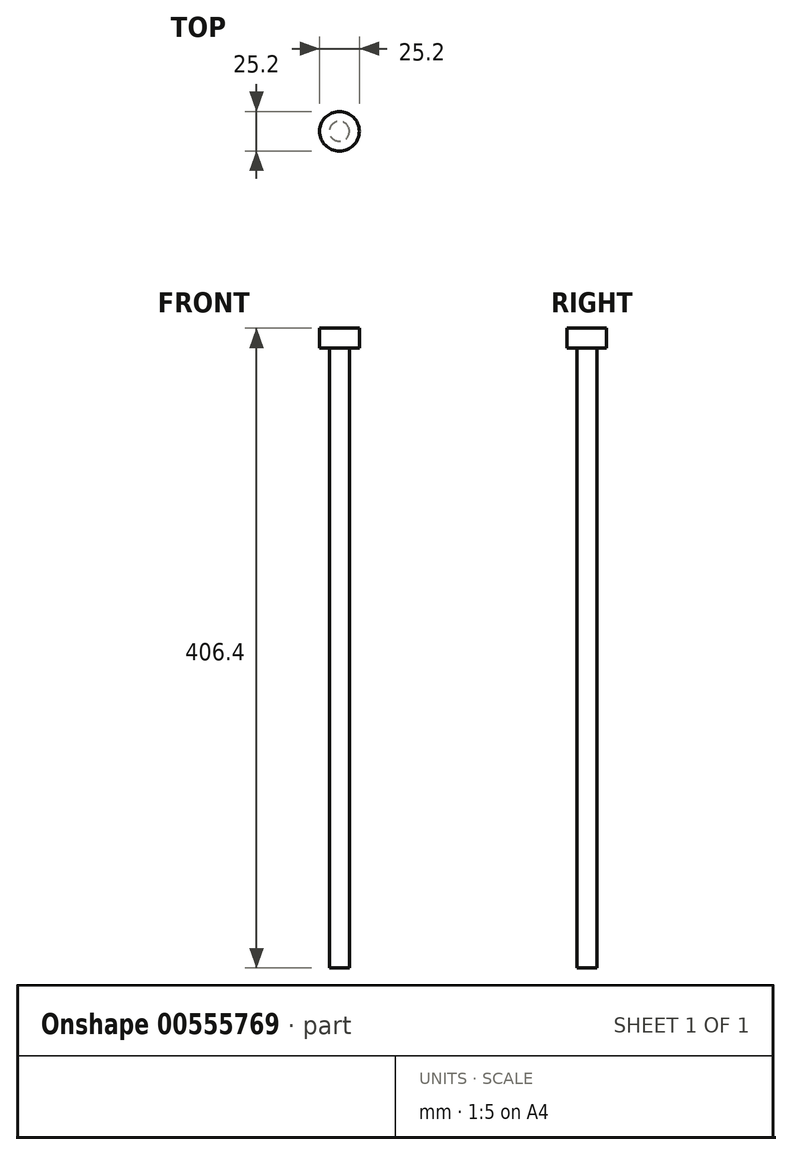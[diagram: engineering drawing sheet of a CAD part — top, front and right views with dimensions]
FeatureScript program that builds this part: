
annotation { "Feature Type Name" : "Feature", "Feature Type Description" : "" }
export const myFeature = defineFeature(function(context is Context, id is Id, definition is map)
    precondition{}
    {
        {
            var Q0;
            Q0=qCreatedBy(makeId("Top.planeOp"),FACE);
            var sketch = newSketch(context, id + "F0", { "sketchPlane" : qUnion([Q0])});
            skCircle(sketch, "E0", {"center": v(0, 0) * mm, "radius": 6.35 * mm});
            skSolve(sketch);
        }
        {
            var Q0;
            Q0 = qSketchRegion(id + "F0", true);
            extrude(context, id + "F1", {"entities" : qUnion([Q0]), "depth" : 406.4 * mm, "offsetDistance" : 25.4 * mm});
        }
        {
            var Q0;
            Q0=makeQuery(id+"F1.opExtrude","CAP_FACE",FACE,{"disambiguationData":[OSD([sQuery(id+"F0.wireOp",EDGE,"E0")])],"isStart":false});
            var sketch = newSketch(context, id + "F2", { "sketchPlane" : qUnion([Q0])});
            skCircle(sketch, "E1", {"center": v(0, 0) * mm, "radius": 12.6 * mm});
            skSolve(sketch);
        }
        {
            var Q0;
            Q0 = qSketchRegion(id + "F2", true);
            extrude(context, id + "F3", {"entities" : qUnion([Q0]), "operationType" : NewBodyOperationType.ADD, "oppositeDirection" : true, "depth" : 12.7 * mm, "offsetDistance" : 25.4 * mm});
        }
    });
